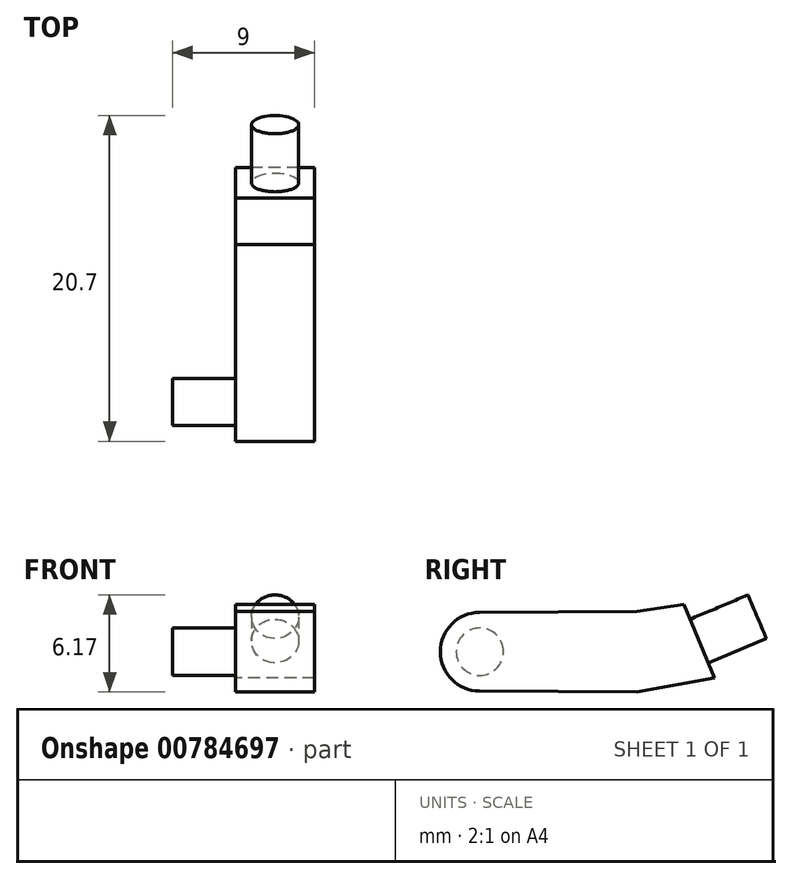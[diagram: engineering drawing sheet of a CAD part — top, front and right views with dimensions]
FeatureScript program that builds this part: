
annotation { "Feature Type Name" : "Feature", "Feature Type Description" : "" }
export const myFeature = defineFeature(function(context is Context, id is Id, definition is map)
    precondition{}
    {
        {
            var Q0;
            Q0=qCreatedBy(makeId("Right.planeOp"),FACE);
            var sketch = newSketch(context, id + "F0", { "sketchPlane" : qUnion([Q0])});
            skLineSegment(sketch, "E0", {"start": v(0, 0) * mm, "end": v(0, -5) * mm});
            skArc(sketch, "E1", {"start": v(0, 0) * mm, "mid": v(-2.49, -2.5) * mm, "end": v(0, -5) * mm});
            skLineSegment(sketch, "E2", {"start": v(0, 0) * mm, "end": v(10, 0.06) * mm});
            skLineSegment(sketch, "E3", {"start": v(0, -5) * mm, "end": v(10, -5.06) * mm});
            skLineSegment(sketch, "E4", {"start": v(10, -5.06) * mm, "end": v(14.92, -4.15) * mm});
            skLineSegment(sketch, "E5", {"start": v(10, 0.06) * mm, "end": v(12.97, 0.51) * mm});
            skLineSegment(sketch, "E6", {"start": v(12.97, 0.51) * mm, "end": v(14.92, -4.15) * mm});
            skSolve(sketch);
        }
        {
            var Q0;
            Q0=makeQuery(id+"F0.imprint","IMPRINT",FACE,{"disambiguationData":[TD([[makeQuery(id+"F0.imprint","IMPRINT",EDGE,{"derivedFrom":sQuery(id+"F0.wireOp",EDGE,"E0")}),1.0]])]});
            var Q1;
            Q1=makeQuery(id+"F0.imprint","IMPRINT",FACE,{"disambiguationData":[TD([[makeQuery(id+"F0.imprint","IMPRINT",EDGE,{"derivedFrom":sQuery(id+"F0.wireOp",EDGE,"E0")}),-1.0]])]});
            extrude(context, id + "F1", {"entities" : qUnion([Q0, Q1]), "depth" : 5 * mm, "offsetDistance" : 25 * mm});
        }
        {
            var Q0;
            Q0=makeQuery(id+"F1.opExtrude","CAP_FACE",FACE,{"disambiguationData":[OSD([sQuery(id+"F0.wireOp",EDGE,"E1"),sQuery(id+"F0.wireOp",EDGE,"E2"),sQuery(id+"F0.wireOp",EDGE,"E3"),sQuery(id+"F0.wireOp",EDGE,"E4"),sQuery(id+"F0.wireOp",EDGE,"E5"),sQuery(id+"F0.wireOp",EDGE,"E6")])],"isStart":true});
            var sketch = newSketch(context, id + "F2", { "sketchPlane" : qUnion([Q0])});
            skCircle(sketch, "E7", {"center": v(-0.01, -2.5) * mm, "radius": 1.5 * mm});
            skSolve(sketch);
        }
        {
            var Q0;
            Q0=makeQuery(id+"F2.imprint","IMPRINT",FACE,{"disambiguationData":[TD([[makeQuery(id+"F2.imprint","IMPRINT",EDGE,{"derivedFrom":sQuery(id+"F2.wireOp",EDGE,"E7")}),1.0]])]});
            extrude(context, id + "F3", {"entities" : qUnion([Q0]), "operationType" : NewBodyOperationType.ADD, "depth" : 4 * mm, "offsetDistance" : 25 * mm});
        }
        {
            var Q0;
            Q0=makeQuery(id+"F1.opExtrude","SWEPT_FACE",FACE,{"disambiguationData":[OSD([sQuery(id+"F0.wireOp",EDGE,"E6")])]});
            var sketch = newSketch(context, id + "F4", { "sketchPlane" : qUnion([Q0])});
            skCircle(sketch, "E8", {"center": v(-2.5, -7.06) * mm, "radius": 1.5 * mm});
            skPoint(sketch, "E8.centerSnap0", {"position": v(0, -7.06) * mm});
            skPoint(sketch, "E8.centerSnap1", {"position": v(-2.5, -4.53) * mm});
            skSolve(sketch);
        }
        {
            var Q0;
            Q0=makeQuery(id+"F4.imprint","IMPRINT",FACE,{"disambiguationData":[TD([[makeQuery(id+"F4.imprint","IMPRINT",EDGE,{"derivedFrom":sQuery(id+"F4.wireOp",EDGE,"E8")}),1.0]])]});
            extrude(context, id + "F5", {"entities" : qUnion([Q0]), "operationType" : NewBodyOperationType.ADD, "depth" : 4 * mm, "offsetDistance" : 25 * mm});
        }
    });
